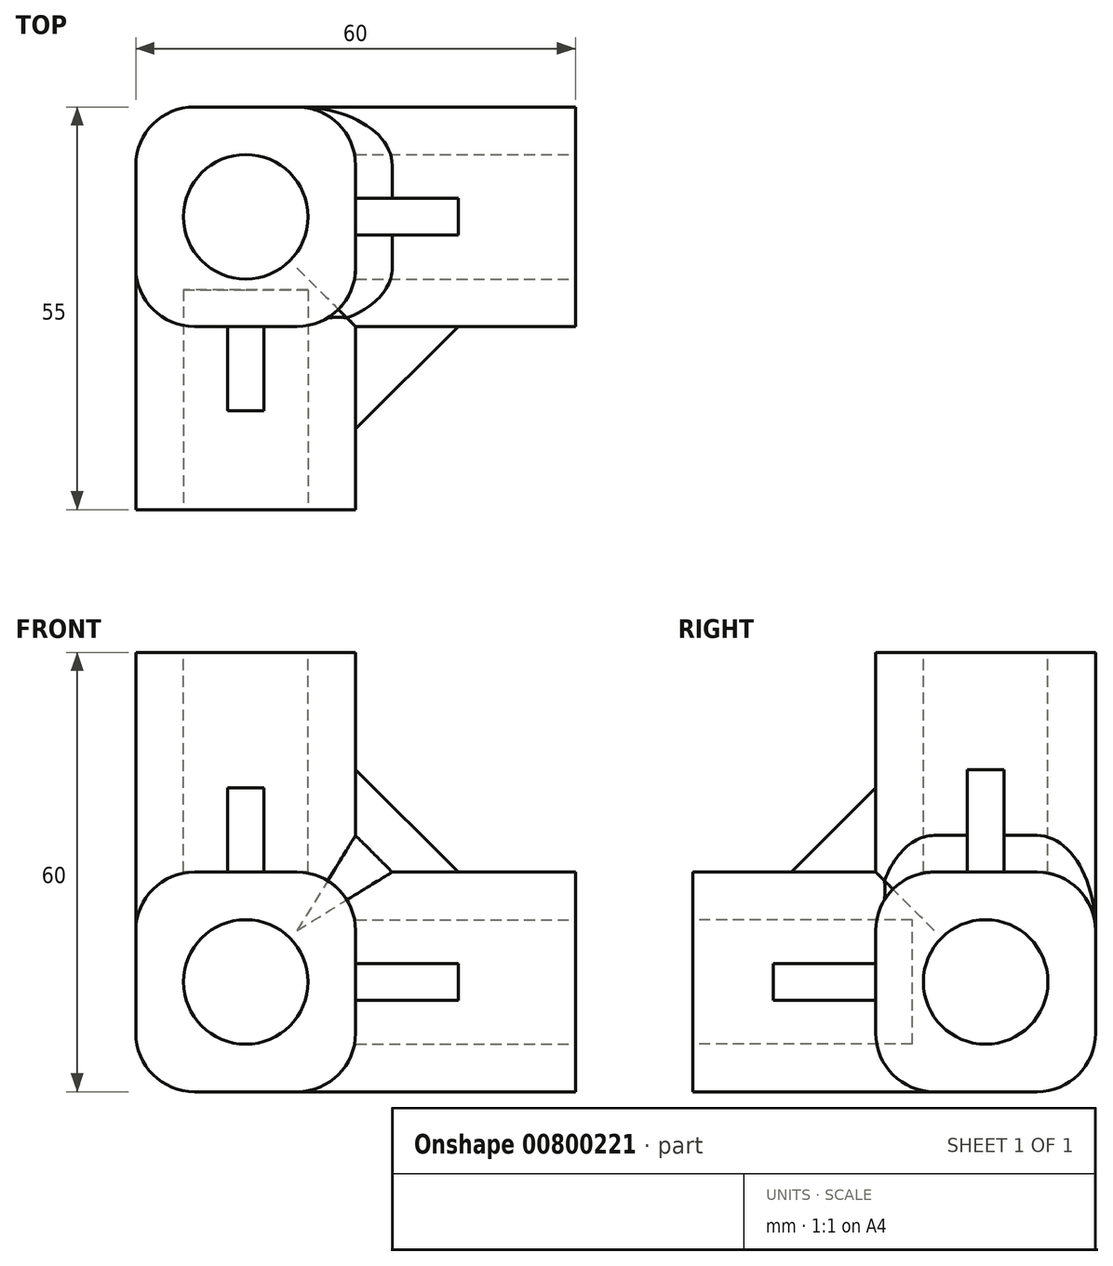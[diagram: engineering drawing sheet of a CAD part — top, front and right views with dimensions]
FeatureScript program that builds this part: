
annotation { "Feature Type Name" : "Feature", "Feature Type Description" : "" }
export const myFeature = defineFeature(function(context is Context, id is Id, definition is map)
    precondition{}
    {
        {
            var Q0;
            Q0=qCreatedBy(makeId("Top.planeOp"),FACE);
            var sketch = newSketch(context, id + "F0", { "sketchPlane" : qUnion([Q0])});
            skLineSegment(sketch, "E0.bottom", {"start": v(-15, 15) * mm, "end": v(15, 15) * mm});
            skLineSegment(sketch, "E0.top", {"start": v(-15, -15) * mm, "end": v(15, -15) * mm});
            skLineSegment(sketch, "E0.left", {"start": v(-15, 15) * mm, "end": v(-15, -15) * mm});
            skLineSegment(sketch, "E0.right", {"start": v(15, 15) * mm, "end": v(15, -15) * mm});
            skSolve(sketch);
        }
        {
            var Q0;
            Q0 = qSketchRegion(id + "F0", true);
            extrude(context, id + "F1", {"entities" : qUnion([Q0]), "depth" : 30 * mm, "offsetDistance" : 25 * mm});
        }
        {
            var Q0;
            Q0=makeQuery(id+"F1.opExtrude","SWEPT_FACE",FACE,{"disambiguationData":[OSD([sQuery(id+"F0.wireOp",EDGE,"E0.top")])]});
            var sketch = newSketch(context, id + "F2", { "sketchPlane" : qUnion([Q0])});
            skLineSegment(sketch, "E1.bottom", {"start": v(-15, 0) * mm, "end": v(15, 0) * mm});
            skLineSegment(sketch, "E1.top", {"start": v(-15, 30) * mm, "end": v(15, 30) * mm});
            skLineSegment(sketch, "E1.left", {"start": v(-15, 0) * mm, "end": v(-15, 30) * mm});
            skLineSegment(sketch, "E1.right", {"start": v(15, 0) * mm, "end": v(15, 30) * mm});
            skSolve(sketch);
        }
        {
            var Q0;
            Q0 = qSketchRegion(id + "F2", true);
            extrude(context, id + "F3", {"entities" : qUnion([Q0]), "operationType" : NewBodyOperationType.ADD, "depth" : 25 * mm, "offsetDistance" : 25 * mm});
        }
        {
            var Q0;
            Q0=makeQuery(id+"F3.opExtrude","CAP_FACE",FACE,{"disambiguationData":[OSD([sQuery(id+"F2.wireOp",EDGE,"E1.bottom"),sQuery(id+"F2.wireOp",EDGE,"E1.top"),sQuery(id+"F2.wireOp",EDGE,"E1.left"),sQuery(id+"F2.wireOp",EDGE,"E1.right")])],"isStart":false});
            var sketch = newSketch(context, id + "F4", { "sketchPlane" : qUnion([Q0])});
            skLineSegment(sketch, "E2", {"start": v(0, 30) * mm, "end": v(0, 0) * mm, "construction": true});
            skCircle(sketch, "E3", {"center": v(0, 15) * mm, "radius": 8.5 * mm});
            skSolve(sketch);
        }
        {
            var Q0;
            Q0 = qSketchRegion(id + "F4", true);
            extrude(context, id + "F5", {"entities" : qUnion([Q0]), "operationType" : NewBodyOperationType.REMOVE, "oppositeDirection" : true, "depth" : 30 * mm, "offsetDistance" : 25 * mm});
        }
        {
            var Q0;
            Q0=makeQuery(id+"F3.boolean.opBoolean","MERGE",FACE,{"derivedFrom":[makeQuery(id+"F1.opExtrude","SWEPT_FACE",FACE,{"disambiguationData":[OSD([sQuery(id+"F0.wireOp",EDGE,"E0.right")])]}),makeQuery(id+"F3.opExtrude","SWEPT_FACE",FACE,{"disambiguationData":[OSD([sQuery(id+"F2.wireOp",EDGE,"E1.right")])]})]});
            var sketch = newSketch(context, id + "F6", { "sketchPlane" : qUnion([Q0])});
            skLineSegment(sketch, "E4.bottom", {"start": v(15, 0) * mm, "end": v(-15, 0) * mm});
            skLineSegment(sketch, "E4.top", {"start": v(15, 30) * mm, "end": v(-15, 30) * mm});
            skLineSegment(sketch, "E4.left", {"start": v(15, 0) * mm, "end": v(15, 30) * mm});
            skLineSegment(sketch, "E4.right", {"start": v(-15, 0) * mm, "end": v(-15, 30) * mm});
            skSolve(sketch);
        }
        {
            var Q0;
            Q0 = qSketchRegion(id + "F6", true);
            extrude(context, id + "F7", {"entities" : qUnion([Q0]), "operationType" : NewBodyOperationType.ADD, "depth" : 30 * mm, "offsetDistance" : 25 * mm});
        }
        {
            var Q0;
            Q0=makeQuery(id+"F7.opExtrude","CAP_FACE",FACE,{"disambiguationData":[OSD([sQuery(id+"F6.wireOp",EDGE,"E4.bottom"),sQuery(id+"F6.wireOp",EDGE,"E4.top"),sQuery(id+"F6.wireOp",EDGE,"E4.left"),sQuery(id+"F6.wireOp",EDGE,"E4.right")])],"isStart":false});
            var sketch = newSketch(context, id + "F8", { "sketchPlane" : qUnion([Q0])});
            skCircle(sketch, "E5", {"center": v(0, 15) * mm, "radius": 8.5 * mm});
            skSolve(sketch);
        }
        {
            var Q0;
            Q0 = qSketchRegion(id + "F8", true);
            extrude(context, id + "F9", {"entities" : qUnion([Q0]), "operationType" : NewBodyOperationType.REMOVE, "oppositeDirection" : true, "depth" : 30 * mm, "offsetDistance" : 25 * mm});
        }
        {
            var Q0;
            Q0=makeQuery(id+"F7.boolean.opBoolean","MERGE",FACE,{"derivedFrom":[makeQuery(id+"F3.boolean.opBoolean","MERGE",FACE,{"derivedFrom":[makeQuery(id+"F1.opExtrude","CAP_FACE",FACE,{"disambiguationData":[OSD([sQuery(id+"F0.wireOp",EDGE,"E0.bottom"),sQuery(id+"F0.wireOp",EDGE,"E0.top"),sQuery(id+"F0.wireOp",EDGE,"E0.left"),sQuery(id+"F0.wireOp",EDGE,"E0.right")])],"isStart":false}),makeQuery(id+"F3.opExtrude","SWEPT_FACE",FACE,{"disambiguationData":[OSD([sQuery(id+"F2.wireOp",EDGE,"E1.top")])]})]}),makeQuery(id+"F7.opExtrude","SWEPT_FACE",FACE,{"disambiguationData":[OSD([sQuery(id+"F6.wireOp",EDGE,"E4.top")])]})]});
            var sketch = newSketch(context, id + "F10", { "sketchPlane" : qUnion([Q0])});
            skLineSegment(sketch, "E6.bottom", {"start": v(-15, 15) * mm, "end": v(15, 15) * mm});
            skLineSegment(sketch, "E6.top", {"start": v(-15, -15) * mm, "end": v(15, -15) * mm});
            skLineSegment(sketch, "E6.left", {"start": v(-15, 15) * mm, "end": v(-15, -15) * mm});
            skLineSegment(sketch, "E6.right", {"start": v(15, 15) * mm, "end": v(15, -15) * mm});
            skSolve(sketch);
        }
        {
            var Q0;
            Q0 = qSketchRegion(id + "F10", true);
            extrude(context, id + "F11", {"entities" : qUnion([Q0]), "operationType" : NewBodyOperationType.ADD, "depth" : 30 * mm, "offsetDistance" : 25 * mm});
        }
        {
            var Q0;
            Q0=makeQuery(id+"F11.opExtrude","CAP_FACE",FACE,{"disambiguationData":[OSD([sQuery(id+"F10.wireOp",EDGE,"E6.bottom"),sQuery(id+"F10.wireOp",EDGE,"E6.top"),sQuery(id+"F10.wireOp",EDGE,"E6.left"),sQuery(id+"F10.wireOp",EDGE,"E6.right")])],"isStart":false});
            var sketch = newSketch(context, id + "F12", { "sketchPlane" : qUnion([Q0])});
            skCircle(sketch, "E7", {"center": v(0, 0) * mm, "radius": 8.5 * mm});
            skSolve(sketch);
        }
        {
            var Q0;
            Q0 = qSketchRegion(id + "F12", true);
            extrude(context, id + "F13", {"entities" : qUnion([Q0]), "operationType" : NewBodyOperationType.REMOVE, "oppositeDirection" : true, "depth" : 30 * mm, "offsetDistance" : 25 * mm});
        }
        {
            var Q0;
            Q0=makeQuery(id+"F11.opExtrude","SWEPT_EDGE",EDGE,{"disambiguationData":[OSD([sQuery(id+"F0.wireOp",EDGE,"E0.left"),sQuery(id+"F2.wireOp",EDGE,"E1.top"),sQuery(id+"F2.wireOp",EDGE,"E1.left"),sQuery(id+"F10.wireOp",EDGE,"E6.top"),sQuery(id+"F10.wireOp",EDGE,"E6.left")])]});
            var Q1;
            Q1=makeQuery(id+"F3.boolean.opBoolean","MERGE",EDGE,{"derivedFrom":[makeQuery(id+"F1.opExtrude","CAP_EDGE",EDGE,{"disambiguationData":[OSD([sQuery(id+"F0.wireOp",EDGE,"E0.left")])],"isStart":false}),makeQuery(id+"F3.opExtrude","SWEPT_EDGE",EDGE,{"disambiguationData":[OSD([sQuery(id+"F2.wireOp",EDGE,"E1.top"),sQuery(id+"F2.wireOp",EDGE,"E1.left")])]})]});
            var Q2;
            Q2=makeQuery(id+"F3.boolean.opBoolean","MERGE",EDGE,{"derivedFrom":[makeQuery(id+"F1.opExtrude","CAP_EDGE",EDGE,{"disambiguationData":[OSD([sQuery(id+"F0.wireOp",EDGE,"E0.left")])],"isStart":true}),makeQuery(id+"F3.opExtrude","SWEPT_EDGE",EDGE,{"disambiguationData":[OSD([sQuery(id+"F2.wireOp",EDGE,"E1.bottom"),sQuery(id+"F2.wireOp",EDGE,"E1.left")])]})]});
            var Q3;
            Q3=makeQuery(id+"F11.boolean.opBoolean","MERGE",EDGE,{"derivedFrom":[makeQuery(id+"F1.opExtrude","SWEPT_EDGE",EDGE,{"disambiguationData":[OSD([sQuery(id+"F0.wireOp",EDGE,"E0.bottom"),sQuery(id+"F0.wireOp",EDGE,"E0.left")])]}),makeQuery(id+"F11.opExtrude","SWEPT_EDGE",EDGE,{"disambiguationData":[OSD([sQuery(id+"F10.wireOp",EDGE,"E6.bottom"),sQuery(id+"F10.wireOp",EDGE,"E6.left")])]})]});
            var Q4;
            Q4=makeQuery(id+"F3.boolean.opBoolean","MERGE",EDGE,{"derivedFrom":[makeQuery(id+"F1.opExtrude","CAP_EDGE",EDGE,{"disambiguationData":[OSD([sQuery(id+"F0.wireOp",EDGE,"E0.right")])],"isStart":true}),makeQuery(id+"F3.opExtrude","SWEPT_EDGE",EDGE,{"disambiguationData":[OSD([sQuery(id+"F2.wireOp",EDGE,"E1.bottom"),sQuery(id+"F2.wireOp",EDGE,"E1.right")])]})]});
            var Q5;
            Q5=makeQuery(id+"F3.boolean.opBoolean","MERGE",EDGE,{"derivedFrom":[makeQuery(id+"F1.opExtrude","CAP_EDGE",EDGE,{"disambiguationData":[OSD([sQuery(id+"F0.wireOp",EDGE,"E0.right")])],"isStart":false}),makeQuery(id+"F3.opExtrude","SWEPT_EDGE",EDGE,{"disambiguationData":[OSD([sQuery(id+"F2.wireOp",EDGE,"E1.top"),sQuery(id+"F2.wireOp",EDGE,"E1.right")])]})]});
            fillet(context, id + "F14", {"entities" : qUnion([Q0, Q1, Q2, Q3, Q4, Q5]), "radius" : 8 * mm, "tangentPropagation" : true, "allowEdgeOverflow" : false});
        }
        {
            var Q0;
            Q0=makeQuery(id+"F11.opExtrude","SWEPT_EDGE",EDGE,{"disambiguationData":[OSD([sQuery(id+"F0.wireOp",EDGE,"E0.right"),sQuery(id+"F2.wireOp",EDGE,"E1.top"),sQuery(id+"F2.wireOp",EDGE,"E1.right"),sQuery(id+"F6.wireOp",EDGE,"E4.top"),sQuery(id+"F6.wireOp",EDGE,"E4.right"),sQuery(id+"F10.wireOp",EDGE,"E6.top"),sQuery(id+"F10.wireOp",EDGE,"E6.right")])]});
            var Q1;
            Q1=makeQuery(id+"F7.opExtrude","SWEPT_EDGE",EDGE,{"disambiguationData":[OSD([sQuery(id+"F0.wireOp",EDGE,"E0.right"),sQuery(id+"F2.wireOp",EDGE,"E1.top"),sQuery(id+"F2.wireOp",EDGE,"E1.right"),sQuery(id+"F6.wireOp",EDGE,"E4.top"),sQuery(id+"F6.wireOp",EDGE,"E4.right")])]});
            var Q2;
            Q2=makeQuery(id+"F11.opExtrude","SWEPT_EDGE",EDGE,{"disambiguationData":[OSD([sQuery(id+"F0.wireOp",EDGE,"E0.bottom"),sQuery(id+"F6.wireOp",EDGE,"E4.top"),sQuery(id+"F6.wireOp",EDGE,"E4.left"),sQuery(id+"F10.wireOp",EDGE,"E6.bottom"),sQuery(id+"F10.wireOp",EDGE,"E6.right")])]});
            var Q3;
            Q3=makeQuery(id+"F7.boolean.opBoolean","MERGE",EDGE,{"derivedFrom":[makeQuery(id+"F1.opExtrude","CAP_EDGE",EDGE,{"disambiguationData":[OSD([sQuery(id+"F0.wireOp",EDGE,"E0.bottom")])],"isStart":false}),makeQuery(id+"F7.opExtrude","SWEPT_EDGE",EDGE,{"disambiguationData":[OSD([sQuery(id+"F6.wireOp",EDGE,"E4.top"),sQuery(id+"F6.wireOp",EDGE,"E4.left")])]})]});
            var Q4;
            Q4=makeQuery(id+"F7.opExtrude","SWEPT_EDGE",EDGE,{"disambiguationData":[OSD([sQuery(id+"F0.wireOp",EDGE,"E0.right"),sQuery(id+"F2.wireOp",EDGE,"E1.bottom"),sQuery(id+"F2.wireOp",EDGE,"E1.right"),sQuery(id+"F6.wireOp",EDGE,"E4.bottom"),sQuery(id+"F6.wireOp",EDGE,"E4.right")])]});
            var Q5;
            Q5=makeQuery(id+"F7.boolean.opBoolean","MERGE",EDGE,{"derivedFrom":[makeQuery(id+"F1.opExtrude","CAP_EDGE",EDGE,{"disambiguationData":[OSD([sQuery(id+"F0.wireOp",EDGE,"E0.bottom")])],"isStart":true}),makeQuery(id+"F7.opExtrude","SWEPT_EDGE",EDGE,{"disambiguationData":[OSD([sQuery(id+"F6.wireOp",EDGE,"E4.bottom"),sQuery(id+"F6.wireOp",EDGE,"E4.left")])]})]});
            fillet(context, id + "F15", {"entities" : qUnion([Q0, Q1, Q2, Q3, Q4, Q5]), "radius" : 8 * mm, "tangentPropagation" : true, "allowEdgeOverflow" : false});
        }
        {
            var Q0;
            Q0=makeQuery(id+"F7.opExtrude","CAP_EDGE",EDGE,{"disambiguationData":[OSD([sQuery(id+"F6.wireOp",EDGE,"E4.right")])],"isStart":true});
            var Q1;
            Q1=makeQuery(id+"F11.opExtrude","CAP_EDGE",EDGE,{"disambiguationData":[OSD([sQuery(id+"F10.wireOp",EDGE,"E6.top")])],"isStart":true});
            var Q2;
            Q2=makeQuery(id+"F11.opExtrude","CAP_EDGE",EDGE,{"disambiguationData":[OSD([sQuery(id+"F10.wireOp",EDGE,"E6.right")])],"isStart":true});
            chamfer(context, id + "F16", {"entities" : qUnion([Q0, Q1, Q2]), "width" : 5 * mm, "tangentPropagation" : true});
        }
        {
            var Q0;
            Q0=qCreatedBy(makeId("Right.planeOp"),FACE);
            var sketch = newSketch(context, id + "F17", { "sketchPlane" : qUnion([Q0])});
            skLineSegment(sketch, "E8", {"start": v(-26.5, 30) * mm, "end": v(-12.5, 44) * mm});
            skLineSegment(sketch, "E9", {"start": v(-12.5, 44) * mm, "end": v(-12.5, 30) * mm});
            skLineSegment(sketch, "E10", {"start": v(-12.5, 30) * mm, "end": v(-26.5, 30) * mm});
            skSolve(sketch);
        }
        {
            var Q0;
            Q0 = qSketchRegion(id + "F17", true);
            extrude(context, id + "F18", {"entities" : qUnion([Q0]), "operationType" : NewBodyOperationType.ADD, "depth" : 2.5 * mm, "offsetDistance" : 25 * mm});
        }
        {
            var Q0;
            Q0 = qSketchRegion(id + "F17", true);
            extrude(context, id + "F19", {"entities" : qUnion([Q0]), "operationType" : NewBodyOperationType.ADD, "oppositeDirection" : true, "depth" : 2.5 * mm, "offsetDistance" : 25 * mm});
        }
        {
            var Q0;
            Q0=qCreatedBy(makeId("Front.planeOp"),FACE);
            var sketch = newSketch(context, id + "F20", { "sketchPlane" : qUnion([Q0])});
            skLineSegment(sketch, "E11", {"start": v(29, 30) * mm, "end": v(15, 44) * mm});
            skLineSegment(sketch, "E12", {"start": v(15, 44) * mm, "end": v(15, 30) * mm});
            skLineSegment(sketch, "E13", {"start": v(15, 30) * mm, "end": v(29, 30) * mm});
            skSolve(sketch);
        }
        {
            var Q0;
            Q0 = qSketchRegion(id + "F20", true);
            extrude(context, id + "F21", {"entities" : qUnion([Q0]), "operationType" : NewBodyOperationType.ADD, "depth" : 2.5 * mm, "offsetDistance" : 25 * mm});
        }
        {
            var Q0;
            Q0 = qSketchRegion(id + "F20", true);
            extrude(context, id + "F22", {"entities" : qUnion([Q0]), "operationType" : NewBodyOperationType.ADD, "oppositeDirection" : true, "depth" : 2.5 * mm, "offsetDistance" : 25 * mm});
        }
        {
            var Q0;
            Q0=qCreatedBy(makeId("Top.planeOp"),FACE);
            cPlane(context, id + "F23", {"entities" : qUnion([Q0]), "cplaneType" : CPlaneType.OFFSET, "offset" : 15 * mm, "width" : 150 * mm, "height" : 150 * mm});
        }
        {
            var Q0;
            Q0=qCreatedBy(id+"F23.planeOp",FACE);
            var sketch = newSketch(context, id + "F24", { "sketchPlane" : qUnion([Q0])});
            skLineSegment(sketch, "E14", {"start": v(15, -29) * mm, "end": v(29, -15) * mm});
            skLineSegment(sketch, "E15", {"start": v(29, -15) * mm, "end": v(15, -15) * mm});
            skLineSegment(sketch, "E16", {"start": v(15, -15) * mm, "end": v(15, -29) * mm});
            skSolve(sketch);
        }
        {
            var Q0;
            Q0 = qSketchRegion(id + "F24", true);
            extrude(context, id + "F25", {"entities" : qUnion([Q0]), "operationType" : NewBodyOperationType.ADD, "depth" : 2.5 * mm, "offsetDistance" : 25 * mm});
        }
        {
            var Q0;
            Q0 = qSketchRegion(id + "F24", true);
            extrude(context, id + "F26", {"entities" : qUnion([Q0]), "operationType" : NewBodyOperationType.ADD, "oppositeDirection" : true, "depth" : 2.5 * mm, "offsetDistance" : 25 * mm});
        }
    });
